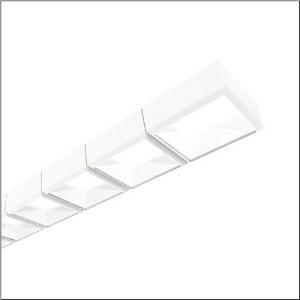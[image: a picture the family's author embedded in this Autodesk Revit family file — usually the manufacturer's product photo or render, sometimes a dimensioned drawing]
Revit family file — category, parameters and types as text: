
# Revit family: scriptus_r__11_5mz214d0twa_b782
name_source: partatom
category: Lighting Fixtures
units: mm (PartAtom-declared; Revit-internal decimal feet)

## family parameters
Cut with Voids When Loaded = No
Host = Face
Light Source = No
Part Type = Normal
Room Calculation Point = No
Round Connector Dimension = Use Diameter
Shared = No

## types (1)
- --- (1 x LED 3000K+6500K / CRI = 80 (unbekannt), 3600 lm, 3000K)
    Apparent Load = 53 VA
    CIE Flux Codes = 82 95 99 100 100
    Color Rendering = 80
    Color Temperature = 3000K
    Default Elevation = 1800 mm
    Description = Scriptus® 11, office luminaire, primary optical cover: lenses, CAT 2 (L<= 3000cd/m²), light emission: direct distribution, primary light characteristic: symmetric, installation type: surface-mounted, LED rated luminous flux: 7.190 lm, light colour: 8tw, colour temperature: 3000..6500K, control gear: ECG DALI, with terminal, 5-pole, mains connection: 230V, AC, 50Hz, rated input power: 53W, housing, luminaire housing, of aluminium, traffic white (RAL 9016), length: 3.088 mm, width: 114 mm, height: 57mm, protection rating (complete): IP20, insulation class (complete): insulation class I (protective earthing), certification: CE, protection symbol: F, permissible ambient temperature for indoor applications: 0..+35°C, standard: EN 50419, packaging unit: 1 piece
    Height = 57 mm
    Lamp = 1 x LED 3000K+6500K / CRI >= 80 (unbekannt)
    Lamp Light Flux = 3600 lm
    Lamp count = 1
    Length = 3088 mm
    Luminous efficacy = 137 lm/W
    Manufacturer = Siteco
    ModVariant = No
    Model = 5MZ214D0TWA
    Mounting Place = Ceiling
    Mounting Type = Surface mounted
    Number of Poles = 1
    OnlyDefault = Yes
    Power Factor = 1
    Product Name = Scriptus® 11
    Product group = office luminaire | ceiling mounted
    ProductGroupID = 302
    Protection Class = Protection class I
    Protection Degree = IP 20
    RLX_Detail_Level = 1
    RlxData = <blob elided: 30425 chars, md5=0c05c939>
    Socket = socket
    Standby Power = 0 W
    System Light Flux = 7200 lm
    System Power = 53 W
    Type Comments = individual setting: colour temperature 6500K
    Type Image = l_1004833.jpg
    URL = http://relux.com
    VarID = @adj_146429
    Voltage = 0 V
    Weight = 0.00 kg
    Width = 114 mm

## geometry (parser evidence)
native form markers: Blend x4, Sweep x14
no freeform markers — native parametric forms only
